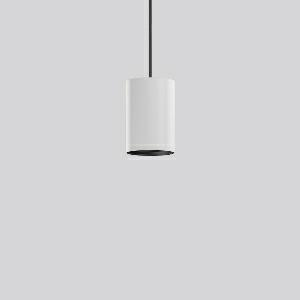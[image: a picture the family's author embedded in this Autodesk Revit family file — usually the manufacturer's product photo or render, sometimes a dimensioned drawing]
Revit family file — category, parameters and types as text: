
# Revit family: deecos_p_maxi_911532_002_b457
name_source: partatom
category: Lighting Fixtures
units: mm (PartAtom-declared; Revit-internal decimal feet)

## family parameters
Cut with Voids When Loaded = No
Host = Face
Light Source = No
Part Type = Normal
Room Calculation Point = No
Round Connector Dimension = Use Diameter
Shared = No

## types (1)
- DEECOS P maxi (1 x LED Modul 930, 3250 lm, 3000)
    Apparent Load = 25 VA
    Approval mark = CE
    CIE Flux Codes = 97 100 100 100 100
    Color Rendering = 90
    Color Temperature = 3000
    Default Elevation = 1800 mm
    Description = Series: DEECOS P maxi
Cylindrical pendant luminaire. Housing: die-cast aluminium, powder-coated. Canopy made of powder-coated sheet steel with magnetic attachment. Optical assembly with reflector made of MIRO-Silver with 98% total light reflection for outstanding efficiency - can be changed without tools. Best colour rendering index Ra>90. Transparent suspension cable 2 m, can be shortened. High quality converter without flickering and stroboscopic effect. The following accessories can be mounted without use of tools: interchangeable lenses, honeycomb louvre, clear and frosted diffusers, white interchangeable plastic ring. Decorative recessed suspension set available as accessory. 
Colour: traffic white, matt (RAL 9016)
Diameter: 123 mm
Height: 181 mm
Suspension length: 2000 mm
Lamp: LED
Socket: without socket
Colour temperature: 3000K
Colour rendering index (CRI): 92
System power: 25 W
Rated luminous flux: 3250 lm
Luminous efficiency: 130 lm/W
Control gear: Regulated power supply
Protection class: I
Type of protection: IP 20
    Height = 181 mm
    Lamp = 1 x LED Modul 930
    Lamp Light Flux = 3250 lm
    Lamp count = 1
    Length = 123 mm
    Lifetime = 50000 h
    Luminous efficacy = 130 lm/W
    Manufacturer = RZB
    ModVariant = No
    Model = 911532.002
    Mounting Place = Ceiling
    Mounting Type = Pendant
    Number of Poles = 1
    OnlyDefault = Yes
    Power Factor = 1
    Product Name = DEECOS P maxi
    Product group = Pendant luminaires
    ProductGroupID = 902
    Protection Class = Protection class I
    Protection Degree = IP 20
    RLX_Detail_Level = 1
    RLX_Emergency_Light_Flux = 0 lm
    RLX_Emergency_Type = 0
    RLX_Emergency_Type_DB = No
    RlxData = <blob elided: 35541 chars, md5=2e2186ae>
    Socket = socket
    Standby Power = 0 W
    System Light Flux = 3250 lm
    System Power = 25 W
    Type Comments = Product without accessories
    Type Image = 911480.002.jpg
    URL = http://relux.com
    VarID = ---
    Voltage = 230 V
    Voltage Range = 220-240 V
    Weight = 0.00 kg
    Width = 0 mm  [stored 0 ft]

note: [stored X ft] marks values corroborated as IEEE doubles in the binary element streams (Revit-internal decimal feet)

## geometry (parser evidence)
native form markers: Blend x4, Sweep x10
no freeform markers — native parametric forms only
